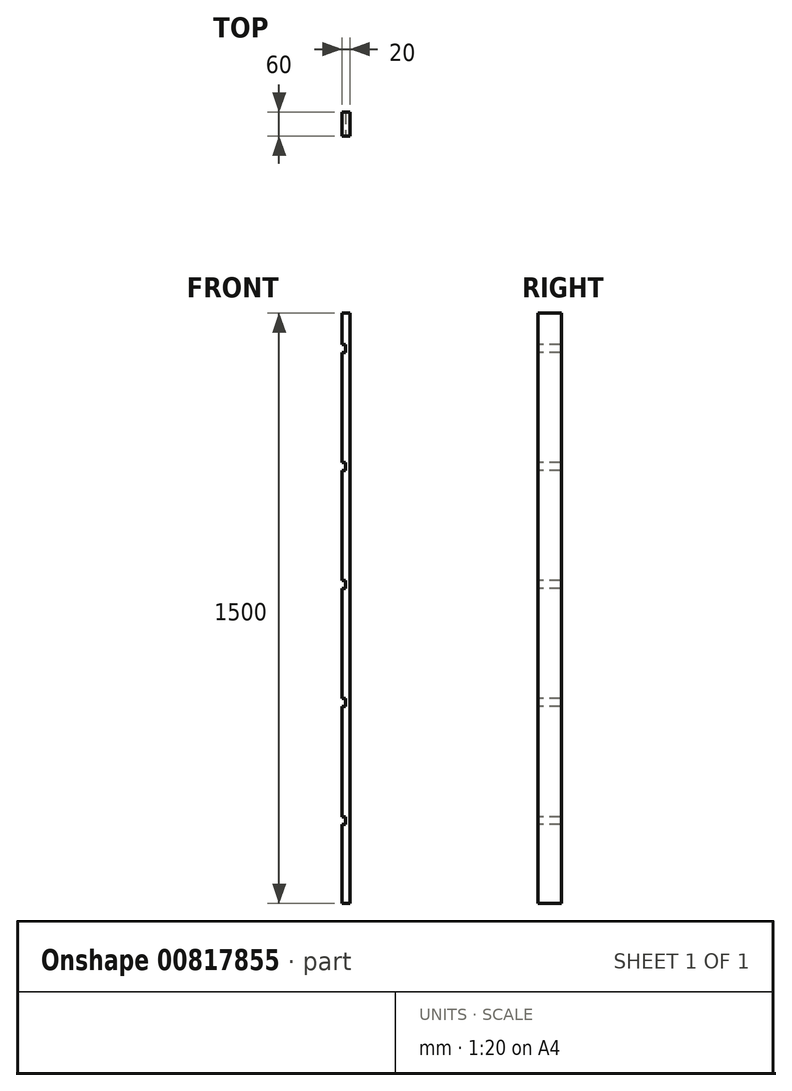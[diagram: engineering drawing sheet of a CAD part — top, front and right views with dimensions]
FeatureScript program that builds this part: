
annotation { "Feature Type Name" : "Feature", "Feature Type Description" : "" }
export const myFeature = defineFeature(function(context is Context, id is Id, definition is map)
    precondition{}
    {
        {
            var Q0;
            Q0=qCreatedBy(makeId("Right.planeOp"),FACE);
            var sketch = newSketch(context, id + "F0", { "sketchPlane" : qUnion([Q0])});
            skLineSegment(sketch, "E0", {"start": v(0, 0) * mm, "end": v(0, 1500) * mm});
            skLineSegment(sketch, "E1", {"start": v(0, 1500) * mm, "end": v(-60, 1500) * mm});
            skLineSegment(sketch, "E2", {"start": v(-60, 1500) * mm, "end": v(-60, 0) * mm});
            skLineSegment(sketch, "E3", {"start": v(-60, 0) * mm, "end": v(0, 0) * mm});
            skSolve(sketch);
        }
        {
            var Q0;
            Q0=makeQuery(id+"F0.imprint","IMPRINT",FACE,{"disambiguationData":[TD([[makeQuery(id+"F0.imprint","IMPRINT",EDGE,{"derivedFrom":sQuery(id+"F0.wireOp",EDGE,"E0")}),1.0]])]});
            extrude(context, id + "F1", {"entities" : qUnion([Q0]), "depth" : 20 * mm, "offsetDistance" : 25 * mm});
        }
        {
            var Q0;
            Q0=makeQuery(id+"F1.opExtrude","CAP_FACE",FACE,{"disambiguationData":[OSD([sQuery(id+"F0.wireOp",EDGE,"E0"),sQuery(id+"F0.wireOp",EDGE,"E1"),sQuery(id+"F0.wireOp",EDGE,"E2"),sQuery(id+"F0.wireOp",EDGE,"E3")])],"isStart":true});
            var sketch = newSketch(context, id + "F2", { "sketchPlane" : qUnion([Q0])});
            skLineSegment(sketch, "E4.bottom", {"start": v(0, 200) * mm, "end": v(60, 200) * mm});
            skLineSegment(sketch, "E4.top", {"start": v(0, 220) * mm, "end": v(60, 220) * mm});
            skLineSegment(sketch, "E4.left", {"start": v(0, 200) * mm, "end": v(0, 220) * mm});
            skLineSegment(sketch, "E4.right", {"start": v(60, 200) * mm, "end": v(60, 220) * mm});
            skLineSegment(sketch, "E5.bottom", {"start": v(0, 500) * mm, "end": v(60, 500) * mm});
            skLineSegment(sketch, "E5.top", {"start": v(0, 520) * mm, "end": v(60, 520) * mm});
            skLineSegment(sketch, "E5.left", {"start": v(0, 500) * mm, "end": v(0, 520) * mm});
            skLineSegment(sketch, "E5.right", {"start": v(60, 500) * mm, "end": v(60, 520) * mm});
            skLineSegment(sketch, "E6.bottom", {"start": v(0, 800) * mm, "end": v(60, 800) * mm});
            skLineSegment(sketch, "E6.top", {"start": v(0, 820) * mm, "end": v(60, 820) * mm});
            skLineSegment(sketch, "E6.left", {"start": v(0, 800) * mm, "end": v(0, 820) * mm});
            skLineSegment(sketch, "E6.right", {"start": v(60, 800) * mm, "end": v(60, 820) * mm});
            skLineSegment(sketch, "E7.bottom", {"start": v(0, 1100) * mm, "end": v(60, 1100) * mm});
            skLineSegment(sketch, "E7.top", {"start": v(0, 1120) * mm, "end": v(60, 1120) * mm});
            skLineSegment(sketch, "E7.left", {"start": v(0, 1100) * mm, "end": v(0, 1120) * mm});
            skLineSegment(sketch, "E7.right", {"start": v(60, 1100) * mm, "end": v(60, 1120) * mm});
            skLineSegment(sketch, "E8.bottom", {"start": v(0, 1400) * mm, "end": v(60, 1400) * mm});
            skLineSegment(sketch, "E8.top", {"start": v(0, 1420) * mm, "end": v(60, 1420) * mm});
            skLineSegment(sketch, "E8.left", {"start": v(0, 1400) * mm, "end": v(0, 1420) * mm});
            skLineSegment(sketch, "E8.right", {"start": v(60, 1400) * mm, "end": v(60, 1420) * mm});
            skSolve(sketch);
        }
        {
            var Q0;
            Q0=makeQuery(id+"F2.imprint","IMPRINT",FACE,{"disambiguationData":[TD([[makeQuery(id+"F2.imprint","IMPRINT",EDGE,{"derivedFrom":sQuery(id+"F2.wireOp",EDGE,"E4.bottom")}),1.0]])]});
            var Q1;
            Q1=makeQuery(id+"F2.imprint","IMPRINT",FACE,{"disambiguationData":[TD([[makeQuery(id+"F2.imprint","IMPRINT",EDGE,{"derivedFrom":sQuery(id+"F2.wireOp",EDGE,"E5.bottom")}),1.0]])]});
            var Q2;
            Q2=makeQuery(id+"F2.imprint","IMPRINT",FACE,{"disambiguationData":[TD([[makeQuery(id+"F2.imprint","IMPRINT",EDGE,{"derivedFrom":sQuery(id+"F2.wireOp",EDGE,"E6.bottom")}),1.0]])]});
            var Q3;
            Q3=makeQuery(id+"F2.imprint","IMPRINT",FACE,{"disambiguationData":[TD([[makeQuery(id+"F2.imprint","IMPRINT",EDGE,{"derivedFrom":sQuery(id+"F2.wireOp",EDGE,"E7.bottom")}),1.0]])]});
            var Q4;
            Q4=makeQuery(id+"F2.imprint","IMPRINT",FACE,{"disambiguationData":[TD([[makeQuery(id+"F2.imprint","IMPRINT",EDGE,{"derivedFrom":sQuery(id+"F2.wireOp",EDGE,"E8.bottom")}),1.0]])]});
            extrude(context, id + "F3", {"entities" : qUnion([Q0, Q1, Q2, Q3, Q4]), "operationType" : NewBodyOperationType.REMOVE, "oppositeDirection" : true, "depth" : 8 * mm, "offsetDistance" : 25 * mm});
        }
    });
